# Revit family: LSTA
name_source: partatom
category: Lighting Fixtures
units: mm (PartAtom-declared; Revit-internal decimal feet)

## family parameters
Always vertical = Yes
Cut with Voids When Loaded = No
Host = Ceiling
Light Source = Yes
OmniClass Number = 23.80.70.11.14.17
OmniClass Title = Direct/Indirect
Part Type = Normal
Room Calculation Point = No
Round Connector Dimension = Use Diameter
Shared = No

## types (11) — shared parameters
Assembly Code = D5020200
Color Filter = 16777215
Description = LED Surfaced Type A
Dimming Lamp Color Temperature Shift = <None>
Emit Shape Visible in Rendering = No
Housing Finish = Metal - Viscor - White
Lamp = LED
Lens Finish = Acrylic - Viscor - Frosted Prismatic P12
Manufacturer = VISIONEERING by VISCOR
Model = LSTA
Tilt Angle = 90.00°
URL = https://www.viscor.com
Voltage = 120 V

## per-type parameters (varying)
| type | Apparent Load | Emit from Rectangle Length | Emit from Rectangle Width | Height | Lamp Wattage | Length | Photometric Web File | Width |
| LSTA1x4-LED840K035LUNV | 30 VA | 3' - 11 3/4" | 0' - 11 3/4" | 0' - 4 5/32" | 30 VA | 3' - 11 3/4" | LSTA1x4-LED840K035LUNV.IES | 0' - 11 3/4" |
| LSTA2X2-LED840K026LUNV | 21 VA | 1' - 11 3/4" | 1' - 11 3/4" | 0' - 3 1/8" | 21 VA | 1' - 11 3/4" | LSTA2X2-LED840K026LUNV.IES | 1' - 11 3/4" |
| LSTA2x4-LED840K040LUNV | 31 VA | 3' - 11 3/4" | 1' - 11 3/4" | 0' - 3 1/8" | 31 VA | 3' - 11 3/4" | LSTA2x4-LED840K040LUNV.IES | 1' - 11 3/4" |
| LSTA1x4-LED840K046LUNV | 35 VA | 3' - 11 3/4" | 0' - 11 3/4" | 0' - 4 5/32" | 35 VA | 3' - 11 3/4" | LSTA1x4-LED840K046LUNV.IES | 0' - 11 3/4" |
| LSTA2x2-LED840K035LUNV | 30 VA | 1' - 11 3/4" | 1' - 11 3/4" | 0' - 3 1/8" | 30 VA | 1' - 11 3/4" | LSTA2x2-LED840K035LUNV.IES | 1' - 11 3/4" |
| LSTA2X2-LED840K040LUNV | 33 VA | 1' - 11 3/4" | 1' - 11 3/4" | 0' - 3 1/8" | 33 VA | 1' - 11 3/4" | LSTA2X2-LED840K040LUNV.IES | 1' - 11 3/4" |
| LSTA2x2-LED840K046LUNV | 38 VA | 1' - 11 3/4" | 1' - 11 3/4" | 0' - 3 1/8" | 38 VA | 1' - 11 3/4" | LSTA2x2-LED840K046LUNV.IES | 1' - 11 3/4" |
| LSTA2x4-LED840K049LUNV | 39 VA | 3' - 11 3/4" | 1' - 11 3/4" | 0' - 3 1/8" | 39 VA | 3' - 11 3/4" | LSTA2x4-LED840K049LUNV.IES | 1' - 11 3/4" |
| LSTA2x4-LED840K063LUNV | 49 VA | 3' - 11 3/4" | 1' - 11 3/4" | 0' - 3 1/8" | 49 VA | 3' - 11 3/4" | LSTA2x4-LED840K063LUNV.IES | 1' - 11 3/4" |
| LSTA2x4-LED840K077LUNV | 60 VA | 3' - 11 3/4" | 1' - 11 3/4" | 0' - 3 1/8" | 60 VA | 3' - 11 3/4" | LSTA2x4-LED840K077LUNV.IES | 1' - 11 3/4" |
| LSTA2x4-LED840K090LUNV | 73 VA | 3' - 11 3/4" | 1' - 11 3/4" | 0' - 3 1/8" | 73 VA | 3' - 11 3/4" | LSTA2x4-LED840K090LUNV.IES | 1' - 11 3/4" |

## geometry (parser evidence)
native form markers: Sweep x3
no freeform markers — native parametric forms only
